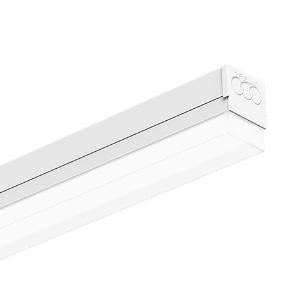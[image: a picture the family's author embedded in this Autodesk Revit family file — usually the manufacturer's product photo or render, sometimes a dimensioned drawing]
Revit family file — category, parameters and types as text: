
# Revit family: 3f_filippi_-_3f_zeta_dr_3f_filippi_-_10967_-_3f_zeta_dr_1x22_led_dali_l1489
name_source: partatom
category: Lighting Fixtures
units: mm (PartAtom-declared; Revit-internal decimal feet)

## family parameters
Cut with Voids When Loaded = No
Host = Face
Light Source = No
Part Type = Normal
Room Calculation Point = No
Round Connector Dimension = Use Diameter
Shared = No

## types (1)
- 3F Filippi - 3F Zeta DR (1 x LED, 3126 lm, 24.5 W, 4000 K)
    Apparent Load = 25 VA
    Approval mark = CE
    CIE Flux Codes = 41 72 91 86 100
    Color Rendering = 80
    Color Temperature = 4000 K
    Control Gear = Electronic transformer
    Default Elevation = 1800 mm
    Description = ILLUMINOTECHNICAL
Luminous efficiency 100% (DLOR 86%, ULOR 14%).
Initial luminous flux of the luminaire 3126 lm.
Diffused symmetric distribution.
Installation Interdistance Transv.D = 1.31 x hu - Long.D = 1.25 x hu.
Tabular UGR (CIE 117 - 4H-8H; S=0.25H; 70/50/20): RUG 23.3 - 21.8.
Beam angle: 136° - 112°.
Luminous efficacy 128 lm/W.
Lifetime (L93/B10): 30000 h. (tq+25°C)
Lifetime (L90/B10): 50000 h. (tq+25°C)
Lifetime (L85/B10): 80000 h. (tq+25°C)
Lifetime (L80/B10): 100000 h. (tq+25°C)
Sudden decreased luminous flux after 50000 hours: 0% (C0).
Photobiological safety in compliance with IEC/TR 62778: RG0 risk exempt, (IEC 62471).
In compliance with IEC/EN 62722-2-1 - IEC/EN 62717 standards.

SOURCE
Linear LED module 22W/840.
Energy efficiency class (UE 2019/2020 - UE 2019/2015): D.
CIE 13.3 Colour rendering index: CRI >80 (R9 <50%).
IES TM-30 Fidelity Index: Rf = 84 Rg = 95.
CCT nominal colour temperature 4000 K.
Colour initial tolerance (MacAdam): SDCM 3.

MECHANICAL
Housing in hot-galvanised steel, painted in white polyester, obtained through rolling process.
Light unit in hot-galvanised steel, painted in white polyester base with fixing springs and retractable safety hooks in stainless steel.
Rectangular screen in self-extinguishing polycarbonate, UV stabilised, opal, with smooth outer surface.
End caps in white polycarbonate.
Pair of stainless steel sliding brackets with sliding block screws.
Luminaire with limited surface temperature. - D - (EN 60598-2-24)
Dimensions: 1489x62 mm, height 81 mm. Weight 3.375 kg.
IP40 protection degree.
Mechanical strength to impacts IK06 (1 joule).
Glow-wire test resistance 850°C.

ELECTRICAL
Halogen Free DALI-2 DATI (Parts 251, 252, 253), PUSH-DIM, electronic wiring 230V-50/60Hz, power factor 0.90 at full load, THD <25%, constant output current, SELV, class I, 1 driver, 1 DALI addresse.
Power of the luminaire 24.5 W.
ENEC - CE.
SAFE FLICKER: PstLM=<1 and SVM=<0.4 (IEC TR 61547-1 and IEC TR 63158), to ensure a more comfortable and safe light.
Luminaire compliant with EN 60598-2-22 for power supply from a centralised emergency system CPSS (Central Power Supply System), not incorporated in the luminaire - high risk areas excluded. The default power and flux are 100% in AC and 15% in DC.
Ambient temperature from 0°C to +25°C.
Temperature class T6 max 85°C.
Relative humidity UR: <85%.

INSTALLATION
Ceiling / Suspended / Wall.
All accessories dedicated to this product are available on the Catalog and on our website www.3F-Filippi.com.

APPLICATIONS
Suitable product for food production plants (HACCP), IFS (Food Version 6), BRC (GSFS Food Version 7).
In commercial environments, exhibition areas, shops and stores.

LIGHT MANAGEMENT
Recommended minimum setting: 10%.
The luminaire, equipped with (DALI-2 DATI) driver, can be controlled manually with 3F Easy Dim technology or automatically/manually with wired or wireless DALI/D2D control systems.
The D2D driver guarantees interoperability with other devices with the same certification by making the following information available:
Device Data (Part 251), Energy Report (Part 252), Diagnosis & Maintenance (Part 253).
In electrical systems without a regulation system (manual or automatic) and DALI bus, a suitable jumper must be made on the DA-DA terminals of the appliance.

WARNING
Luminaire designed for disposal/recycling at end-of-life.
Replaceable (LED only) light source by a professional. Replaceable control gear by a professional.
    Height = 81 mm
    Lamp = 1 x LED
    Lamp Light Flux = 3126 lm
    Lamp Power = 24.5 W
    Lamp count = 1
    Length = 1489 mm
    Lifetime = 50000 h
    Luminous efficacy = 128 lm/W
    Manufacturer = 3F Filippi
    ModVariant = No
    Model = 3F Filippi - 10967 - 3F Zeta DR 1x22 LED DALI L1489
    Mounting Place = Ceiling
    Mounting Type = Pendant
    Number of Poles = 1
    OnlyDefault = Yes
    Power Factor = 1
    Product Name = 3F Filippi - 3F Zeta DR
    Product group = pendant luminaire
    ProductGroupID = 9
    Protection Class = Protection class I
    Protection Degree = IP 40
    RLX_Detail_Level = 1
    RLX_Emergency_Light_Flux = 0 lm
    RLX_Emergency_Type = 0
    RLX_Emergency_Type_DB = No
    RlxData = <blob elided: 35385 chars, md5=faecdbe9>
    Socket = socket
    Standby Power = 0 W
    System Light Flux = 3126 lm
    System Power = 25 W
    Type Comments = Product without accessories
    Type Image = 3ffilippi_3f_zeta_dr.jpg
    URL = http://relux.com
    VarID = ---
    Voltage = 0 V
    Weight = 0.00 kg
    Width = 62 mm  [stored 0.203412 ft]

note: [stored X ft] marks values corroborated as IEEE doubles in the binary element streams (Revit-internal decimal feet)

## geometry (parser evidence)
native form markers: Blend x4, Sweep x14
no freeform markers — native parametric forms only
